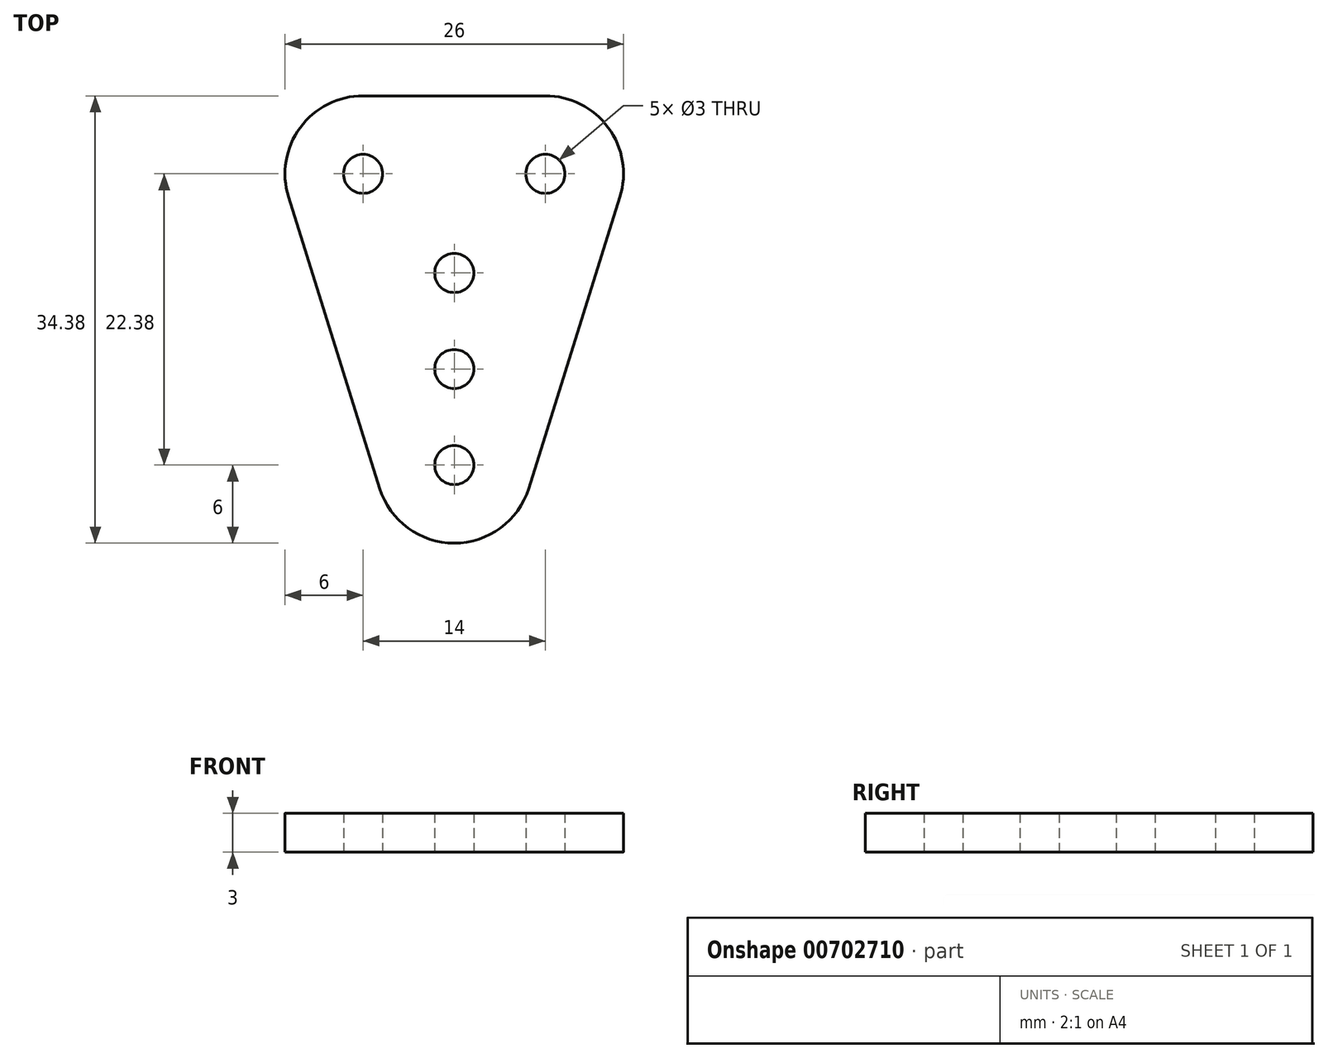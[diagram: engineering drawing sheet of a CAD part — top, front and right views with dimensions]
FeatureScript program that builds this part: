
annotation { "Feature Type Name" : "Feature", "Feature Type Description" : "" }
export const myFeature = defineFeature(function(context is Context, id is Id, definition is map)
    precondition{}
    {
        {
            var Q0;
            Q0=qCreatedBy(makeId("Top.planeOp"),FACE);
            var sketch = newSketch(context, id + "F0", { "sketchPlane" : qUnion([Q0])});
            skCircle(sketch, "E0", {"center": v(0, 0) * mm, "radius": 1.5 * mm});
            skCircle(sketch, "E1", {"center": v(14, 0) * mm, "radius": 1.5 * mm});
            skLineSegment(sketch, "E2", {"start": v(0, 0) * mm, "end": v(14, 0) * mm, "construction": true});
            skLineSegment(sketch, "E3", {"start": v(7, 0) * mm, "end": v(7, -15) * mm, "construction": true});
            skCircle(sketch, "E4", {"center": v(7, -7.62) * mm, "radius": 1.5 * mm});
            skCircle(sketch, "E5", {"center": v(7, -22.38) * mm, "radius": 1.5 * mm});
            skArc(sketch, "E6", {"start": v(0, 6) * mm, "mid": v(-4.83, 3.55) * mm, "end": v(-5.73, -1.8) * mm});
            skArc(sketch, "E7", {"start": v(19.73, -1.8) * mm, "mid": v(18.83, 3.55) * mm, "end": v(14, 6) * mm});
            skArc(sketch, "E8", {"start": v(1.27, -24.17) * mm, "mid": v(7, -28.38) * mm, "end": v(12.73, -24.17) * mm});
            skLineSegment(sketch, "E9", {"start": v(0, 6) * mm, "end": v(14, 6) * mm});
            skLineSegment(sketch, "E10", {"start": v(19.73, -1.8) * mm, "end": v(12.73, -24.17) * mm});
            skLineSegment(sketch, "E11", {"start": v(1.27, -24.17) * mm, "end": v(-5.73, -1.8) * mm});
            skCircle(sketch, "E12", {"center": v(7, -15) * mm, "radius": 1.5 * mm});
            skSolve(sketch);
        }
        {
            var Q0;
            Q0=makeQuery(id+"F0.imprint","IMPRINT",FACE,{"disambiguationData":[TD([[makeQuery(id+"F0.imprint","IMPRINT",EDGE,{"derivedFrom":sQuery(id+"F0.wireOp",EDGE,"E0")}),-1.0]])]});
            extrude(context, id + "F1", {"entities" : qUnion([Q0]), "depth" : 3 * mm, "offsetDistance" : 25.4 * mm});
        }
    });
